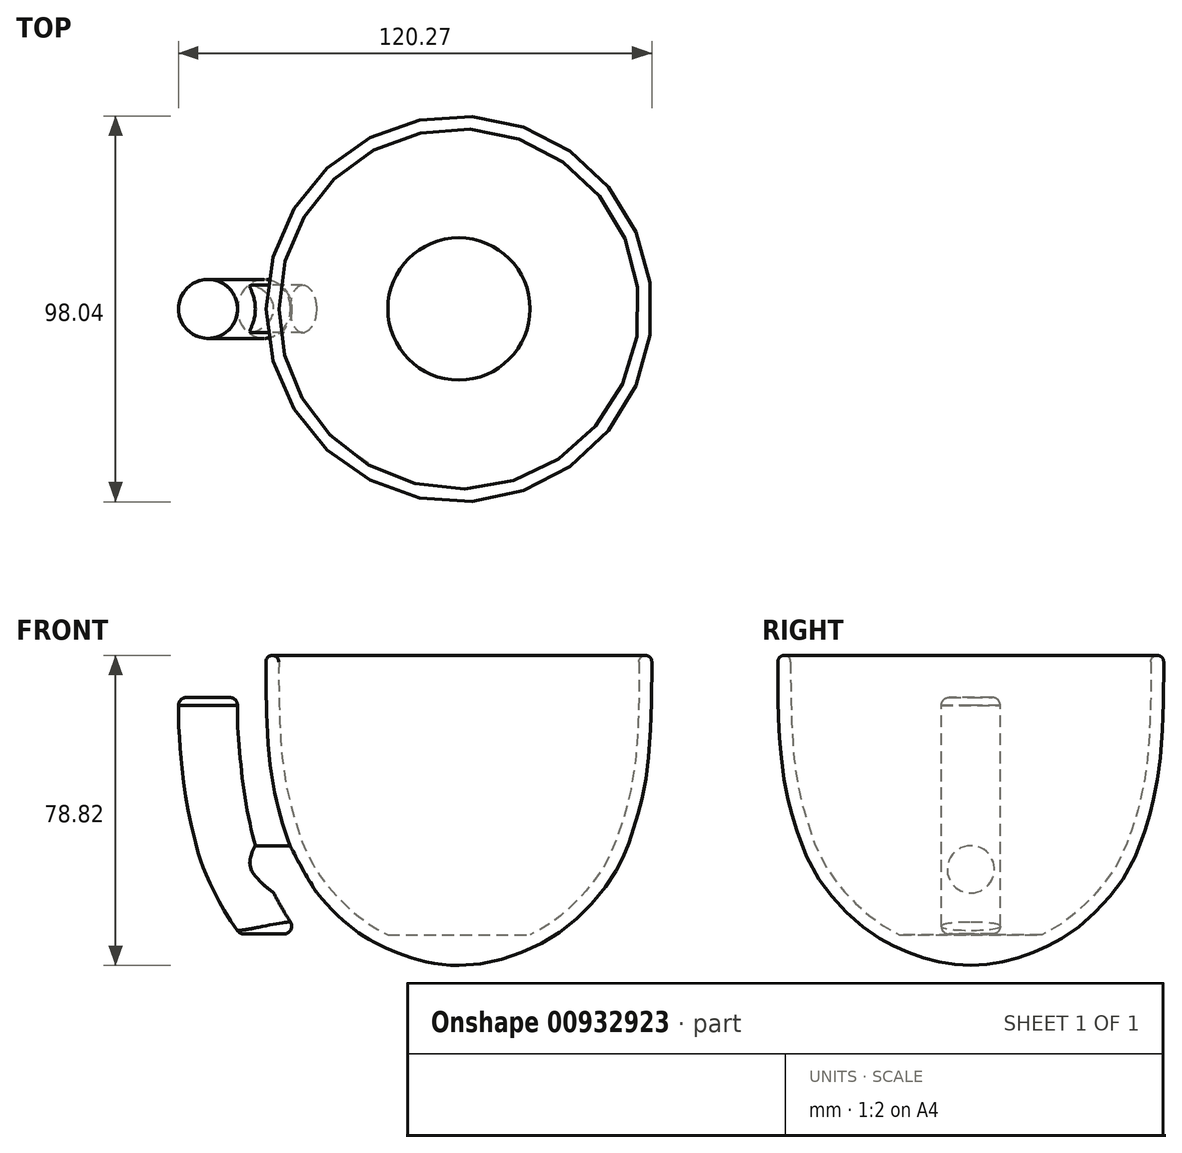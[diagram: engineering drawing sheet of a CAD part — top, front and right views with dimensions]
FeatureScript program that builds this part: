
annotation { "Feature Type Name" : "Feature", "Feature Type Description" : "" }
export const myFeature = defineFeature(function(context is Context, id is Id, definition is map)
    precondition{}
    {
        {
            var Q0;
            Q0=qCreatedBy(makeId("Front.planeOp"),FACE);
            var sketch = newSketch(context, id + "F0", { "sketchPlane" : qUnion([Q0])});
            skLineSegment(sketch, "E0", {"start": v(0, 78.82) * mm, "end": v(-49, 78.82) * mm});
            skLineSegment(sketch, "E1", {"start": v(0, 0) * mm, "end": v(0, 78.82) * mm});
            skFitSpline(sketch, "E2", {"points": [v(-49, 78.82) * mm, v(-49, 71.2) * mm, v(-47.95, 50.94) * mm, v(-44.24, 34.32) * mm, v(-38.54, 21.8) * mm, v(-27.37, 9.77) * mm, v(-17.3, 3.96) * mm, v(0, 0) * mm], "startDerivative": vector(-0.53, -120.05) * mm, "endDerivative": vector(126.32, 0) * mm});
            skSolve(sketch);
        }
        {
            var Q0;
            Q0=qSketchRegion(id+"F0",true);
            var Q1;
            Q1=sQuery(id+"F0.wireOp",EDGE,"E1");
            revolve(context, id + "F1", {"surfaceOperationType" : NewSurfaceOperationType.NEW, "entities" : qUnion([Q0]), "axis" : qUnion([Q1]), "revolveType" : RevolveType.FULL});
        }
        {
            var Q0;
            Q0=makeQuery(id+"F1.opRevolve","SWEPT_FACE",FACE,{"disambiguationData":[OSD([sQuery(id+"F0.wireOp",EDGE,"E0")])]});
            shell(context, id + "F2", {"entities" : qUnion([Q0]), "thickness" : 3.25 * mm});
        }
        {
            var Q0;
            Q0=makeQuery(id+"F1.opRevolve","SWEPT_EDGE",EDGE,{"disambiguationData":[OSD([sQuery(id+"F0.wireOp",EDGE,"E0"),sQuery(id+"F0.wireOp",EDGE,"E2")])]});
            var Q1;
            Q1=makeQuery(id+"F2.opShell","OFFSET_EDGE",EDGE,{"disambiguationData":[OSD([sQuery(id+"F0.wireOp",EDGE,"E0"),sQuery(id+"F0.wireOp",EDGE,"E2")])]});
            fillet(context, id + "F3", {"entities" : qUnion([Q0, Q1]), "radius" : (3.25 / 2) * mm, "tangentPropagation" : true, "defaultsChanged" : true, "vertexSettings" : [], "allowEdgeOverflow" : false});
        }
        {
            var Q0;
            Q0=qCreatedBy(makeId("Front.planeOp"),FACE);
            var sketch = newSketch(context, id + "F4", { "sketchPlane" : qUnion([Q0])});
            skLineSegment(sketch, "E3", {"start": v(-41.77, 30.38) * mm, "end": v(-53.43, 30.38) * mm});
            skLineSegment(sketch, "E4", {"start": v(-49.23, 20.12) * mm, "end": v(-36.53, 20.12) * mm});
            skLineSegment(sketch, "E5", {"start": v(-36.53, 20.12) * mm, "end": v(-41.77, 30.38) * mm});
            skFitSpline(sketch, "E6", {"points": [v(-42.03, 8) * mm, v(-47.44, 16.94) * mm, v(-49.23, 20.12) * mm, v(-51.33, 24.44) * mm, v(-53.43, 30.38) * mm, v(-55.23, 38.72) * mm, v(-56.67, 49.18) * mm, v(-57.32, 61.86) * mm, v(-57.58, 68.13) * mm, v(-57.6, 68.09) * mm], "startDerivative": vector(-47.1, 69.03) * mm, "endDerivative": vector(-6.03, -13.35) * mm});
            skLineSegment(sketch, "E7", {"start": v(-57.58, 68.13) * mm, "end": v(-69.83, 68.13) * mm});
            skFitSpline(sketch, "E8", {"points": [v(-69.83, 68.13) * mm, v(-69.83, 61.07) * mm, v(-69.06, 51.29) * mm, v(-67.63, 40.46) * mm, v(-65.54, 31.18) * mm, v(-63.64, 25) * mm, v(-58.64, 14.66) * mm, v(-54.3, 8) * mm], "startDerivative": vector(-1.12, -53.42) * mm, "endDerivative": vector(31.44, -44.67) * mm});
            skLineSegment(sketch, "E9", {"start": v(-54.3, 8) * mm, "end": v(-42.03, 8) * mm});
            skSolve(sketch);
        }
        {
            var Q0;
            Q0=qCreatedBy(makeId("Right.planeOp"),FACE);
            cPlane(context, id + "F5", {"entities" : qUnion([Q0]), "cplaneType" : CPlaneType.OFFSET, "offset" : 55 * mm, "oppositeDirection" : true, "width" : 150 * mm, "height" : 150 * mm});
        }
        {
            var Q0;
            Q0=qCreatedBy(id+"F5.planeOp",FACE);
            var sketch = newSketch(context, id + "F6", { "sketchPlane" : qUnion([Q0])});
            skPoint(sketch, "E10.middle", {"position": v(0, 24.44) * mm});
            skCircle(sketch, "E11", {"center": v(0, 24.44) * mm, "radius": 6 * mm});
            skSolve(sketch);
        }
        {
            var Q0;
            Q0=qSketchRegion(id+"F6",true);
            extrude(context, id + "F7", {"entities" : qUnion([Q0]), "operationType" : NewBodyOperationType.ADD, "endBound" : BoundingType.UP_TO_NEXT, "depth" : 25 * mm, "offsetDistance" : 25 * mm});
        }
        {
            var Q0;
            Q0=qCreatedBy(makeId("Top.planeOp"),FACE);
            cPlane(context, id + "F8", {"entities" : qUnion([Q0]), "cplaneType" : CPlaneType.OFFSET, "offset" : 8 * mm, "width" : 150 * mm, "height" : 150 * mm});
        }
        {
            var Q0;
            Q0=qCreatedBy(id+"F8.planeOp",FACE);
            var sketch = newSketch(context, id + "F9", { "sketchPlane" : qUnion([Q0])});
            skPoint(sketch, "E12.middle", {"position": v(-48.17, 0) * mm});
            skCircle(sketch, "E13", {"center": v(-48.17, 0) * mm, "radius": 7.5 * mm});
            skSolve(sketch);
        }
        {
            var Q0;
            Q0=qSketchRegion(id+"F9",true);
            var Q1;
            Q1=sQuery(id+"F4.wireOp",EDGE,"E8");
            sweep(context, id + "F10", {"operationType" : NewBodyOperationType.ADD, "profiles" : qUnion([Q0]), "path" : qUnion([Q1]), "keepProfileOrientation" : true});
        }
        {
            var Q0;
            Q0=makeQuery(id+"F10.opSweep","CAP_FACE",FACE,{"disambiguationData":[OSD([sQuery(id+"F4.wireOp",VERTEX,"E8.start"),sQuery(id+"F9.wireOp",EDGE,"E12.bottom"),sQuery(id+"F9.wireOp",EDGE,"E12.top"),sQuery(id+"F9.wireOp",EDGE,"E12.left"),sQuery(id+"F9.wireOp",EDGE,"E12.right")])],"isStart":false});
            var Q1;
            Q1=makeQuery(id+"F10.opSweep","CAP_FACE",FACE,{"disambiguationData":[OSD([sQuery(id+"F4.wireOp",VERTEX,"E8.end"),sQuery(id+"F9.wireOp",EDGE,"E12.bottom"),sQuery(id+"F9.wireOp",EDGE,"E12.top"),sQuery(id+"F9.wireOp",EDGE,"E12.left"),sQuery(id+"F9.wireOp",EDGE,"E12.right")])],"isStart":true});
            fillet(context, id + "F11", {"entities" : qUnion([Q0, Q1]), "radius" : 2 * mm, "tangentPropagation" : true, "allowEdgeOverflow" : false});
        }
        {
            var Q0;
            Q0=qCreatedBy(makeId("Front.planeOp"),FACE);
            var sketch = newSketch(context, id + "F12", { "sketchPlane" : qUnion([Q0])});
            skLineSegment(sketch, "E14", {"start": v(0, 1.35) * mm, "end": v(0, 7.85) * mm});
            skLineSegment(sketch, "E15", {"start": v(0, 7.85) * mm, "end": v(-21, 7.85) * mm});
            skLineSegment(sketch, "E16", {"start": v(-21, 7.85) * mm, "end": v(0, 1.35) * mm});
            skSolve(sketch);
        }
        {
            var Q0;
            Q0=qSketchRegion(id+"F12",true);
            var Q1;
            Q1=sQuery(id+"F12.wireOp",EDGE,"E14");
            revolve(context, id + "F13", {"operationType" : NewBodyOperationType.ADD, "surfaceOperationType" : NewSurfaceOperationType.NEW, "entities" : qUnion([Q0]), "axis" : qUnion([Q1]), "revolveType" : RevolveType.FULL});
        }
    });
